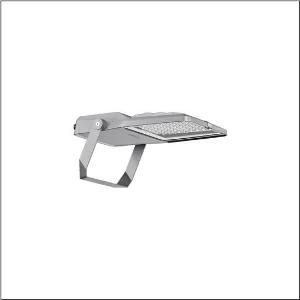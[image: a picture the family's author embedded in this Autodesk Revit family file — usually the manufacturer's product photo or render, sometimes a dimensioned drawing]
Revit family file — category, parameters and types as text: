
# Revit family: floodlight_fl_21_mini___pl61_5xa7776b2c1a_e1cc
name_source: partatom
category: Lighting Fixtures
units: mm (PartAtom-declared; Revit-internal decimal feet)

## family parameters
Cut with Voids When Loaded = No
Host = Face
Light Source = No
Part Type = Normal
Room Calculation Point = No
Round Connector Dimension = Use Diameter
Shared = No

## types (1)
- --- (1 x LED, 6110 lm, 45.7 W, 3000K)
    Apparent Load = 46 VA
    CIE Flux Codes = 33 65 98 100 100
    Color Rendering = 70
    Color Temperature = 3000K
    Default Elevation = 1800 mm
    Description = Floodlight FL 21 mini, floodlight, primary light control with lens, of PMMA, primary optical cover: protective disc, of toughened safety glass, transparent, light distribution: PL61, light emission: direct distribution, installation type: surface-mounted, LED, High Power LED, rated luminous flux: 6.110lm, luminous efficacy: 134lm/W, light colour: 730, colour temperature: 3000K, control gear: Smart Interface (Zhaga), control: flexible luminous flux parameterisation, time-dependent luminous flux control, constant luminous flux control, overheat protection, pre-setting: logarithmic dimming characteristic, with terminal, 6-pole, mains connection: 220..240V, AC, 50/60Hz, start of lifetime: 46W, end of service life: 48W, reduction: 22W, luminaire housing, of diecast aluminium, powder-coated, SITECO metallic grey (DB 702S), corrosivity category C5 mid according to DIN EN ISO 12944, suitable for swimming pools, chlorine-resistant, sealing non-destructively replaceable, mounting bracket, of steel, galvanised, powder-coated, SITECO metallic grey (DB 702S), Smart Interface below and above, protection rating (complete): IP66, insulation class (complete): insulation class II (safety insulation), certification: CE, ENEC, VDE, protection symbol: D, impact resistance: IK08, permissible operating ambient temperature: -40..+40°C, permissible operating ambient temperature for outdoor applications: -40..+50°C, standard: DIN EN 12944, LABS conformity tested according to VDMA 24364:2018-05, packaging unit: 1 piece

Light Distribution: PL61
    Height = 70 mm
    Lamp = 1 x LED
    Lamp Light Flux = 6110 lm
    Lamp Power = 45.7 W
    Lamp count = 1
    Length = 485 mm
    Luminous efficacy = 134 lm/W
    Manufacturer = Siteco
    ModVariant = No
    Model = 5XA7776B2C1A
    Mounting Place = Pole
    Mounting Type = Pole annexe
    Number of Poles = 1
    OnlyDefault = Yes
    Power Factor = 1
    Product Name = Floodlight FL 21 mini | PL61
    Product group = floodlight | pylon annexe
    ProductGroupID = 6201
    Protection Class = Protection class II
    Protection Degree = IP 66
    RLX_Detail_Level = 1
    RLX_Emergency_Light_Flux = 0 lm
    RLX_Emergency_Type = 0
    RLX_Emergency_Type_DB = No
    RlxData = <blob elided: 96089 chars, md5=434f698b>
    Socket = socket
    Standby Power = 0 W
    System Light Flux = 6110 lm
    System Power = 46 W
    Type Comments = factory setting: luminous flux: 100 % | dim-lin: 254 | 463 mA
    Type Image = l_1006845.jpg
    URL = http://relux.com
    VarID = @adj_173201
    Voltage = 0 V
    Weight = 0.00 kg
    Width = 337 mm

## geometry (parser evidence)
native form markers: Blend x4, Sweep x11
no freeform markers — native parametric forms only
